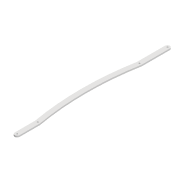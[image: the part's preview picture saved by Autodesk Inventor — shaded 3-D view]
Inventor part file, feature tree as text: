
AUTODESK INVENTOR PART (.ipt)
format: ipt  version: 2022 (Build 260153000, 153)  size: 107,008 bytes
history: native  units: mm
features: extrude x1, sketch x1
ambient origin geometry x8: Origin, YZ Plane, XZ Plane, XY Plane, X Axis, Y Axis, Z Axis, Center Point
bodies: Solid1 (feature_tree)
feature tree (2):
  extrude  "Extrusion1"  Depth=600.0mm
  sketch  "Sketch1"  dims[d0=3.3mm d1=3.3mm d2=10.0mm d3=312.648mm d6=3.0mm d7=0.0mm d10=3.3mm d11=42.6mm d12=3.3mm d13=254.274mm d16=600.0mm d17=600.0mm]
